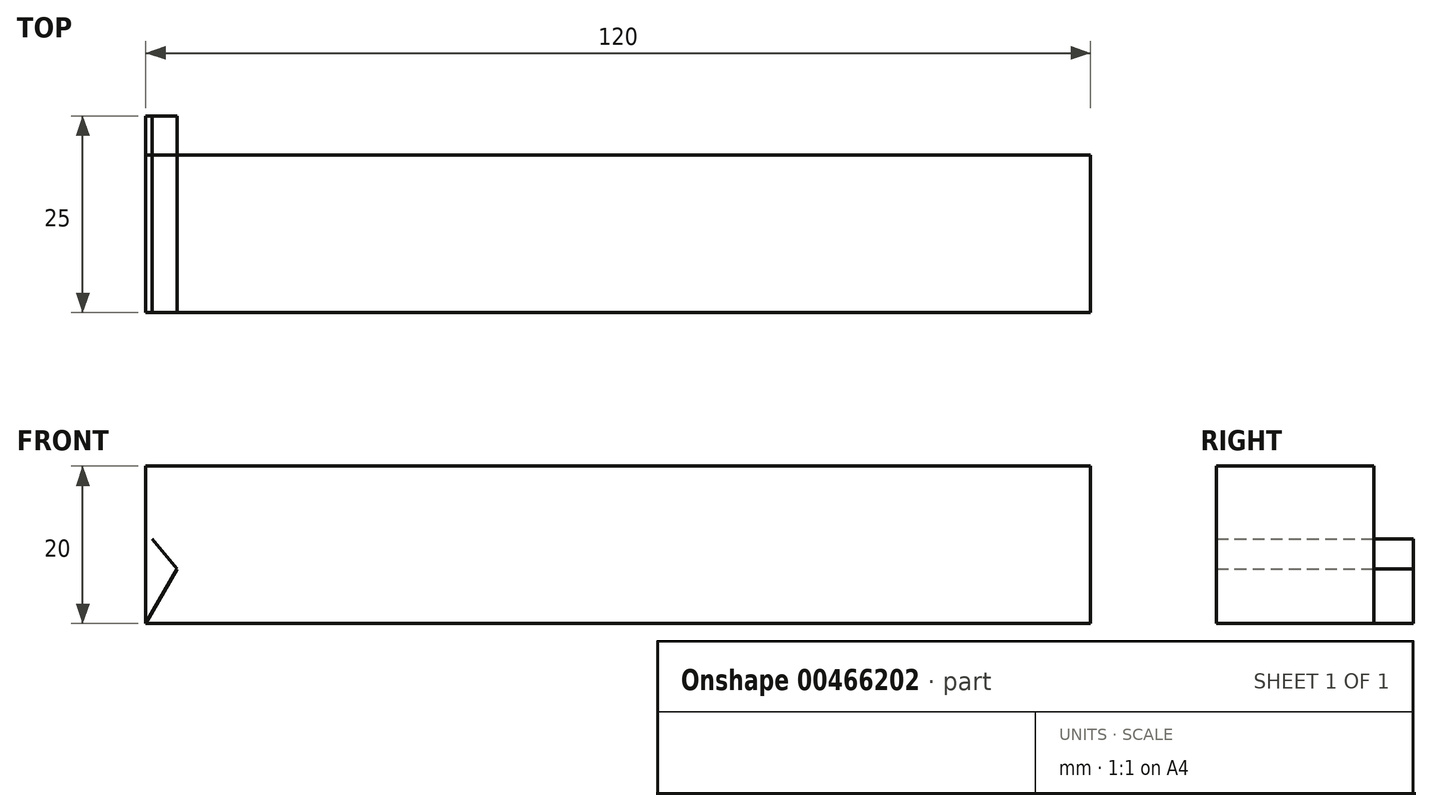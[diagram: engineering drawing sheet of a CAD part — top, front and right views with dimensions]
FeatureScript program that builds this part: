
annotation { "Feature Type Name" : "Feature", "Feature Type Description" : "" }
export const myFeature = defineFeature(function(context is Context, id is Id, definition is map)
    precondition{}
    {
        {
            var Q0;
            Q0=qCreatedBy(makeId("Front.planeOp"),FACE);
            var sketch = newSketch(context, id + "F0", { "sketchPlane" : qUnion([Q0])});
            skLineSegment(sketch, "E0", {"start": v(0, 0) * mm, "end": v(120, 0) * mm});
            skLineSegment(sketch, "E1", {"start": v(120, 0) * mm, "end": v(120, 20) * mm});
            skSolve(sketch);
        }
        {
            var Q0;
            Q0=sQuery(id+"F0.wireOp",EDGE,"E0");
            var Q1;
            Q1=sQuery(id+"F0.wireOp",EDGE,"E1");
            extrude(context, id + "F1", {"bodyType" : ToolBodyType.SURFACE, "surfaceEntities" : qUnion([Q0, Q1]), "depth" : 20 * mm});
        }
        {
            var Q0;
            Q0=makeQuery(id+"F1.opExtrude","SWEPT_FACE",FACE,{"disambiguationData":[OSD([sQuery(id+"F0.wireOp",EDGE,"E0")])]});
            var sketch = newSketch(context, id + "F2", { "sketchPlane" : qUnion([Q0])});
            skLineSegment(sketch, "E2.1", {"start": v(120, 20) * mm, "end": v(0, 20) * mm});
            skLineSegment(sketch, "E3.0", {"start": v(0, 0) * mm, "end": v(120, 0) * mm});
            skSolve(sketch);
        }
        {
            var Q0;
            Q0 = qSketchRegion(id + "F2", true);
            var Q1;
            Q1 = qConstructionFilter(qBodyType(qCreatedBy(id + "F2" ,EDGE), BodyType.WIRE), ConstructionObject.NO);
            extrude(context, id + "F3", {"entities" : qUnion([Q0]), "bodyType" : ToolBodyType.SURFACE, "surfaceEntities" : qUnion([Q1]), "oppositeDirection" : true, "depth" : 20 * mm});
        }
        {
            var Q0;
            Q0=makeQuery(id+"F3.opExtrude","SWEPT_FACE",FACE,{"disambiguationData":[OSD([sQuery(id+"F2.wireOp",EDGE,"E2.1")])]});
            var sketch = newSketch(context, id + "F4", { "sketchPlane" : qUnion([Q0])});
            skLineSegment(sketch, "E4", {"start": v(0, 0) * mm, "end": v(-4, 6.93) * mm});
            skLineSegment(sketch, "E5", {"start": v(-4, 6.93) * mm, "end": v(-0.79, 10.76) * mm});
            skSolve(sketch);
        }
        {
            var Q0;
            Q0 = qSketchRegion(id + "F4", true);
            var Q1;
            Q1 = qConstructionFilter(qBodyType(qCreatedBy(id + "F4" ,EDGE), BodyType.WIRE), ConstructionObject.NO);
            extrude(context, id + "F5", {"entities" : qUnion([Q0]), "bodyType" : ToolBodyType.SURFACE, "surfaceEntities" : qUnion([Q1]), "depth" : 25 * mm});
        }
    });
